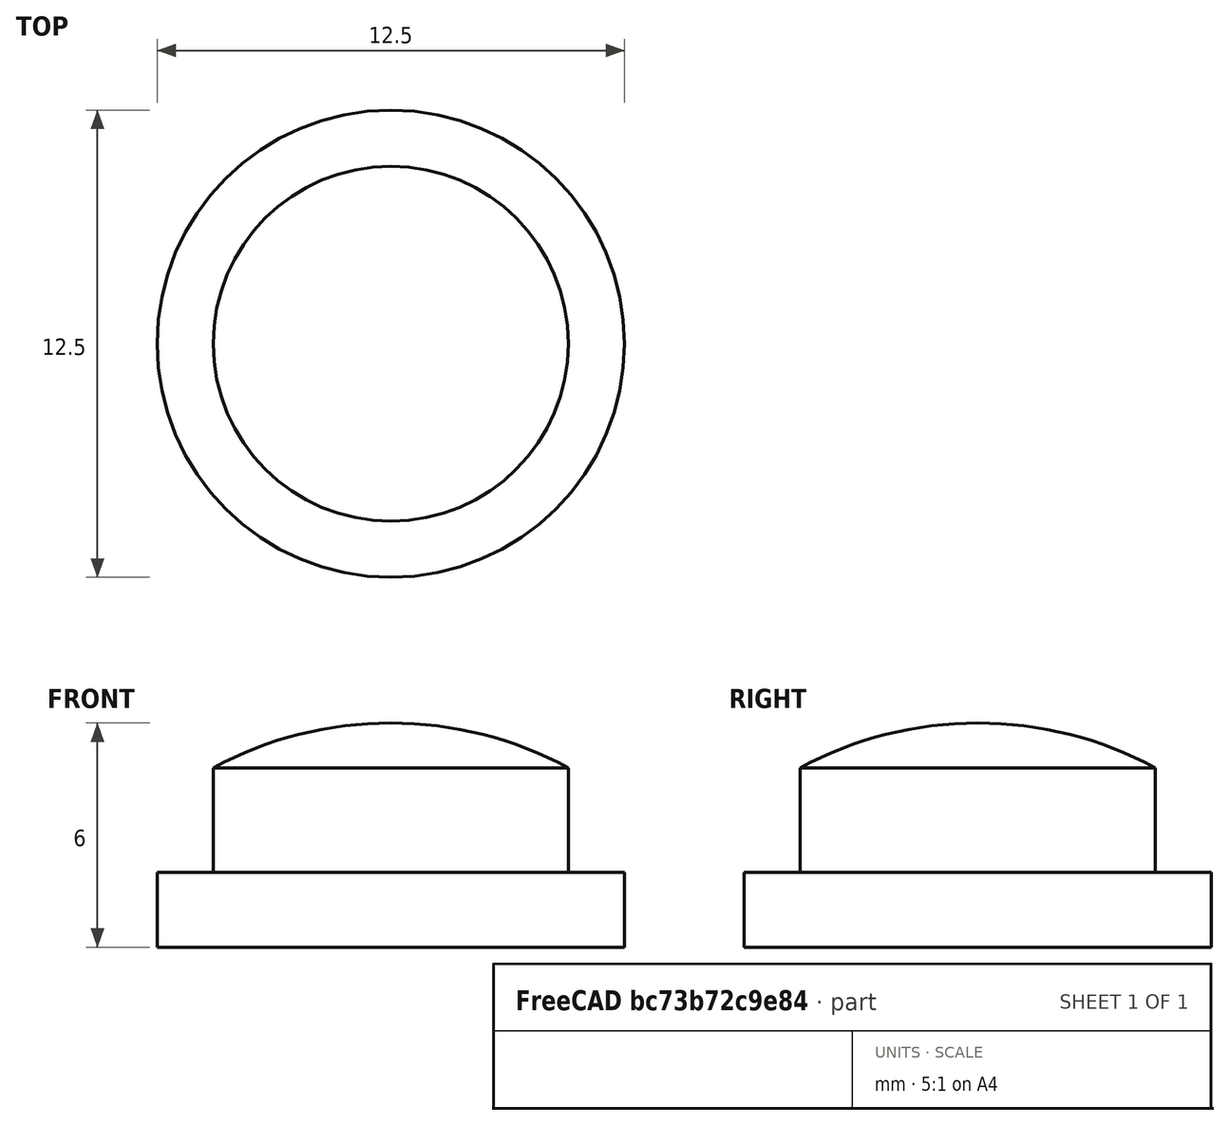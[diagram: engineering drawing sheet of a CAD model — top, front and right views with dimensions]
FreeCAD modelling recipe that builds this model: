
FCSTD DOCUMENT  (FreeCAD 0.22R34542 (Git))
Label: Kindertuer_Knopf
License: All rights reserved
LicenseURL: https://en.wikipedia.org/wiki/All_rights_reserved
objects: TechDraw::DrawViewDimension×7, TechDraw::DrawProjGroupItem×2, Sketcher::SketchObject×1, PartDesign::Revolution×1, PartDesign::Body×1, TechDraw::DrawSVGTemplate×1, TechDraw::DrawProjGroup×1, TechDraw::DrawPage×1
note: 13 computed .brp shape members not serialized (recipe doc carries the construction recipe); baked Part::Feature solids carry a one-line shape summary decoded from their .brp

FEATURE [Sketcher::SketchObject] Sketch
  FullyConstrained = true
  MapMode = 5
  Placement = pos=(0,0,0) rot=(1,0,0;1.5708rad)
  Support = -> [XZ_Plane]
  expr: Constraints[15] = 9.5 / 2
  expr: Constraints[17] = 12.5 / 2
  sketch-geometry (6):
    g0: LineSegment StartX=0 StartY=0 StartZ=0 EndX=6.25 EndY=0 EndZ=0
    g1: LineSegment StartX=6.25 StartY=0 StartZ=0 EndX=6.25 EndY=2 EndZ=0
    g2: LineSegment StartX=6.25 StartY=2 StartZ=0 EndX=4.75 EndY=2 EndZ=0
    g3: LineSegment StartX=4.75 StartY=2 StartZ=0 EndX=4.75 EndY=4.79986 EndZ=0
    g4: LineSegment StartX=0 StartY=0 StartZ=0 EndX=6e-16 EndY=6 EndZ=0
    g5: ArcOfCircle CenterX=0 CenterY=-4 CenterZ=0 NormalX=0 NormalY=0 NormalZ=1 AngleXU=0 Radius=10 StartAngle=1.07583 EndAngle=1.5708
  constraints (18):
    c: Coincident(g-1,g0)
    c: PointOnObject(g0,g-1)
    c: Coincident(g0,g1)
    c: Vertical(g1)
    c: Coincident(g1,g2)
    c: Horizontal(g2)
    c: Coincident(g2,g3)
    c: Vertical(g3)
    c: Coincident(g0,g4)
    c: PointOnObject(g4,g-2)
    c: PointOnObject(g5,g4)
    c: Coincident(g5,g4)
    c: Coincident(g3,g5)
    c: DistanceY(g0,g4) = 6
    c: DistanceY(g1) = 2
    c: DistanceX(g4,g3) = 4.75
    c: Radius(g5) = 10
    c: DistanceX(g0,g0) = 6.25
FEATURE [PartDesign::Revolution] Revolution
  Angle = 360
  Axis = (0,2e-16,1)
  Base = (0,0,0)
  Placement = pos=(0,0,0) rot=(1,0,0;1.5708rad)
  Profile = -> Sketch
  ReferenceAxis = -> Sketch [V_Axis]
  Reversed = true
FEATURE [PartDesign::Body] Body  label="Knopf"
  Group = -> [Sketch,Revolution]
  Origin = -> Origin
  Tip = -> Revolution
FEATURE [TechDraw::DrawSVGTemplate] Template  label="Vorlage"
  EditableTexts = Designed_by_Name=Designed by Name; Drawing_number=Drawing number; FC-Date=Date; FC-SC=Scale; FC-SH=Sheet; FC-Title=Title; Subtitle=Subtitle; Weight=Weight
  Height = 210
  Orientation = 1
  Template = /snap/freecad/793/usr/share/Mod/TechDraw/Templates/A4_LandscapeTD.svg
  Width = 297
FEATURE [TechDraw::DrawProjGroupItem] ProjItem  label="Vorderansicht"
  CoarseView = false
  Direction = (0,-1,0)
  Focus = 100
  HardHidden = false
  IsoCount = 0
  IsoHidden = false
  IsoVisible = false
  LockPosition = true
  Perspective = false
  Rotation = 0
  RotationVector = (1,0,0)
  Scale = 5
  ScaleType = 2
  ScrubCount = 0
  SeamHidden = false
  SeamVisible = false
  SmoothHidden = false
  SmoothVisible = true
  Source = -> [Revolution]
  Type = 0
  X = 0
  XDirection = (1,0,0)
  Y = 0
FEATURE [TechDraw::DrawProjGroupItem] ProjItem001  label="Draufsicht"
  CoarseView = false
  Direction = (0,0,1)
  Focus = 100
  HardHidden = false
  IsoCount = 0
  IsoHidden = false
  IsoVisible = false
  LockPosition = false
  Perspective = false
  Rotation = 0
  RotationVector = (1,0,0)
  Scale = 5
  ScaleType = 2
  ScrubCount = 0
  SeamHidden = false
  SeamVisible = false
  SmoothHidden = false
  SmoothVisible = true
  Source = -> [Revolution]
  Type = 4
  X = 0
  XDirection = (1,0,0)
  Y = -74.0298
FEATURE [TechDraw::DrawProjGroup] ProjGroup
  Anchor = -> ProjItem
  AutoDistribute = false
  LockPosition = false
  ProjectionType = 0
  Rotation = 0
  Scale = 5
  ScaleType = 0
  Source = -> [Revolution]
  Views = -> [ProjItem,ProjItem001]
  X = 96.1042
  Y = 152.552
  spacingX = 25
  spacingY = 15
FEATURE [TechDraw::DrawViewDimension] Dimension  label="Maß"
  AngleOverride = false
  Arbitrary = false
  ArbitraryTolerances = false
  EqualTolerance = true
  ExtensionAngle = 0
  FormatSpec = ⌀%.2w
  FormatSpecOverTolerance = %+.2w
  FormatSpecUnderTolerance = %+.2w
  Inverted = false
  LineAngle = 0
  LockPosition = false
  MeasureType = 1
  OverTolerance = 0
  References2D = -> [ProjItem001]
  Rotation = 0
  Scale = 5
  ScaleType = 0
  TheoreticalExact = false
  Type = 5
  UnderTolerance = 0
  X = 0
  Y = 0
FEATURE [TechDraw::DrawViewDimension] Dimension001  label="Maß001"
  AngleOverride = false
  Arbitrary = false
  ArbitraryTolerances = false
  EqualTolerance = true
  ExtensionAngle = 0
  FormatSpec = ⌀%.2w
  FormatSpecOverTolerance = %+.2w
  FormatSpecUnderTolerance = %+.2w
  Inverted = false
  LineAngle = 0
  LockPosition = false
  MeasureType = 1
  OverTolerance = 0
  References2D = -> [ProjItem]
  Rotation = 0
  Scale = 5
  ScaleType = 0
  TheoreticalExact = false
  Type = 1
  UnderTolerance = 0
  X = -0.491936
  Y = 29.9469
FEATURE [TechDraw::DrawViewDimension] Dimension002  label="Maß002"
  AngleOverride = false
  Arbitrary = false
  ArbitraryTolerances = false
  EqualTolerance = true
  ExtensionAngle = 0
  FormatSpec = ⌀%.2w
  FormatSpecOverTolerance = %+.2w
  FormatSpecUnderTolerance = %+.2w
  Inverted = false
  LineAngle = 0
  LockPosition = false
  MeasureType = 1
  OverTolerance = 0
  References2D = -> [ProjItem]
  Rotation = 0
  Scale = 5
  ScaleType = 0
  TheoreticalExact = false
  Type = 1
  UnderTolerance = 0
  X = -1.47581
  Y = 41.367
FEATURE [TechDraw::DrawViewDimension] Dimension003  label="Maß003"
  AngleOverride = false
  Arbitrary = false
  ArbitraryTolerances = false
  EqualTolerance = true
  ExtensionAngle = 0
  FormatSpec = %.2w
  FormatSpecOverTolerance = %+.2w
  FormatSpecUnderTolerance = %+.2w
  Inverted = false
  LineAngle = 0
  LockPosition = false
  MeasureType = 1
  OverTolerance = 0
  References2D = -> [ProjItem]
  Rotation = 0
  Scale = 5
  ScaleType = 0
  TheoreticalExact = false
  Type = 2
  UnderTolerance = 0
  X = 36.4153
  Y = -7.00806
FEATURE [TechDraw::DrawViewDimension] Dimension004  label="Maß004"
  AngleOverride = false
  Arbitrary = false
  ArbitraryTolerances = false
  EqualTolerance = true
  ExtensionAngle = 0
  FormatSpec = %.2w
  FormatSpecOverTolerance = %+.2w
  FormatSpecUnderTolerance = %+.2w
  Inverted = false
  LineAngle = 0
  LockPosition = false
  MeasureType = 1
  OverTolerance = 0
  References2D = -> [ProjItem]
  Rotation = 0
  Scale = 5
  ScaleType = 0
  TheoreticalExact = false
  Type = 2
  UnderTolerance = 0
  X = 48.5041
  Y = -5.91165
FEATURE [TechDraw::DrawViewDimension] Dimension005  label="Maß005"
  AngleOverride = false
  Arbitrary = false
  ArbitraryTolerances = false
  EqualTolerance = true
  ExtensionAngle = 0
  FormatSpec = %.2w
  FormatSpecOverTolerance = %+.2w
  FormatSpecUnderTolerance = %+.2w
  Inverted = false
  LineAngle = 0
  LockPosition = false
  MeasureType = 1
  OverTolerance = 0
  References2D = -> [ProjItem]
  Rotation = 0
  Scale = 5
  ScaleType = 0
  TheoreticalExact = false
  Type = 2
  UnderTolerance = 0
  X = 58.6694
  Y = 1.7621
FEATURE [TechDraw::DrawViewDimension] Dimension006  label="Maß006"
  AngleOverride = false
  Arbitrary = false
  ArbitraryTolerances = false
  EqualTolerance = true
  ExtensionAngle = 0
  FormatSpec = R%.2w
  FormatSpecOverTolerance = %+.2w
  FormatSpecUnderTolerance = %+.2w
  Inverted = false
  LineAngle = 0
  LockPosition = false
  MeasureType = 1
  OverTolerance = 0
  References2D = -> [ProjItem]
  Rotation = 0
  Scale = 5
  ScaleType = 0
  TheoreticalExact = false
  Type = 4
  UnderTolerance = 0
  X = 6.25528
  Y = 4.17019
FEATURE [TechDraw::DrawPage] Page  label="Seite"
  KeepUpdated = true
  NextBalloonIndex = 1
  ProjectionType = 0
  Scale = 5
  Template = -> Template
  Views = -> [ProjGroup,Dimension,Dimension001,Dimension002,Dimension003,Dimension004,Dimension005,Dimension006]
